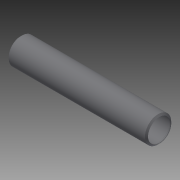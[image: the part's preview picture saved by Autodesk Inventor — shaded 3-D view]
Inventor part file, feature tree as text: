
AUTODESK INVENTOR PART (.ipt)
format: ipt  version: 2014 (Build 180170000, 170)  size: 120,832 bytes
history: native  units: in
note: dims shown in document units (in); Inventor stores cm internally (conversion verified against a paired STEP export)
features: other x56, revolve x1, sketch x1
ambient origin geometry x8: Origin, YZ Plane, XZ Plane, XY Plane, X Axis, Y Axis, Z Axis, Center Point
bodies: Solid1 (feature_tree)
feature tree (58):
  revolve  "Revolution1"  [1 undecoded]
  other  "o1_XY"
  other  "o1_YZ"
  other  "o1_ZX"
  other  "o1_X"
  other  "o1_Y"
  other  "o1_Z"
  other  "o1_Center"
  other  "o2_XY"
  other  "o2_YZ"
  other  "o2_ZX"
  other  "o2_X"
  other  "o2_Y"
  other  "o2_Z"
  other  "o2_Center"
  other  "t1_XY"
  other  "t1_YZ"
  other  "t1_ZX"
  other  "t1_X"
  other  "t1_Y"
  other  "t1_Z"
  other  "t1_Center"
  other  "t2_XY"
  other  "t2_YZ"
  other  "t2_ZX"
  other  "t2_X"
  other  "t2_Y"
  other  "t2_Z"
  other  "t2_Center"
  other  "t3_XY"
  other  "t3_YZ"
  other  "t3_ZX"
  other  "t3_X"
  other  "t3_Y"
  other  "t3_Z"
  other  "t3_Center"
  other  "t4_XY"
  other  "t4_YZ"
  other  "t4_ZX"
  other  "t4_X"
  other  "t4_Y"
  other  "t4_Z"
  other  "t4_Center"
  other  "tube1_XY"
  other  "tube1_YZ"
  other  "tube1_ZX"
  other  "tube1_X"
  other  "tube1_Y"
  other  "tube1_Z"
  other  "tube1_Center"
  other  "tube2_XY"
  other  "tube2_YZ"
  other  "tube2_ZX"
  other  "tube2_X"
  other  "tube2_Y"
  other  "tube2_Z"
  other  "tube2_Center"
  sketch  "Sketch_5"  dims[d0=360.0deg]
note: 1 required parameter value undecoded (feature->parameter linkage not recoverable at this tier; creation-order binding heuristic only, values carry confidence <= 0.55)
